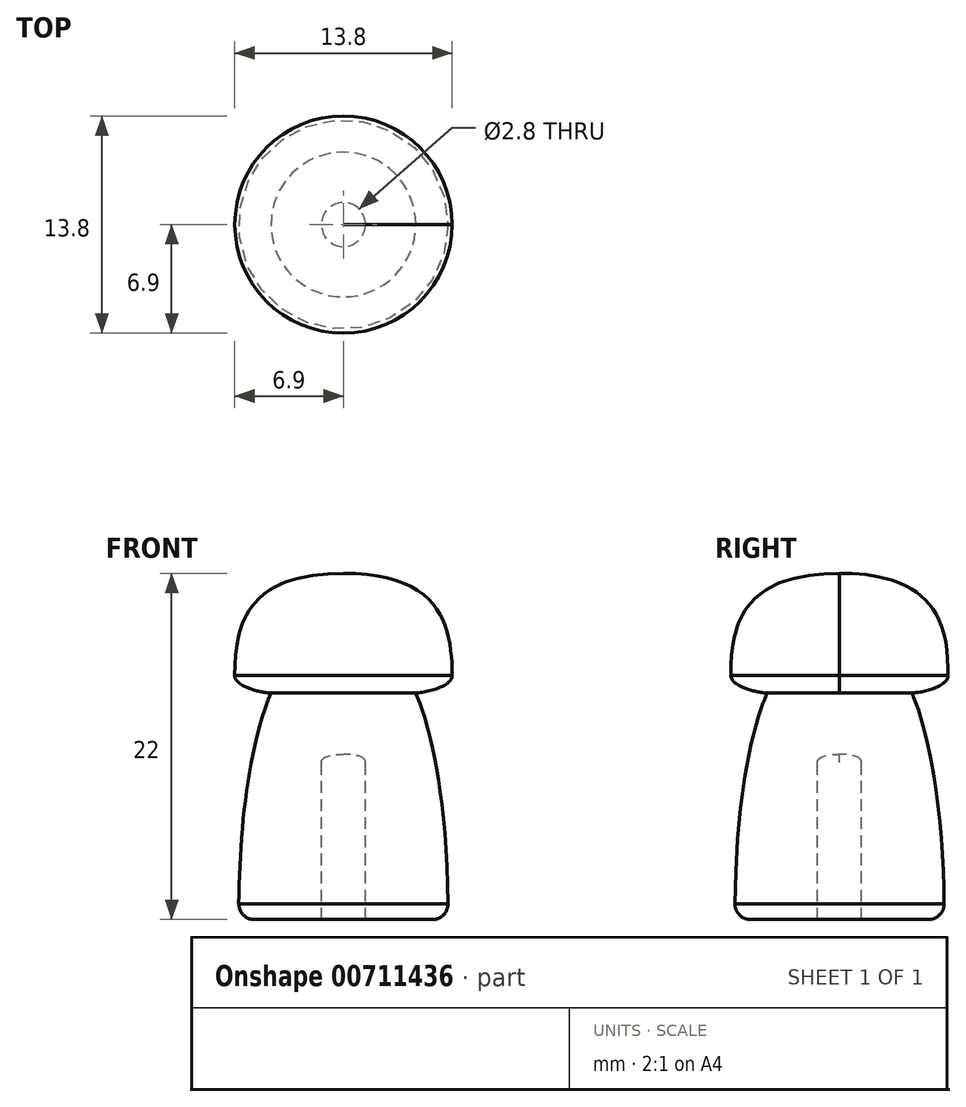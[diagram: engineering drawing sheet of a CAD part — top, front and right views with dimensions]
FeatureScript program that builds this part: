
annotation { "Feature Type Name" : "Feature", "Feature Type Description" : "" }
export const myFeature = defineFeature(function(context is Context, id is Id, definition is map)
    precondition{}
    {
        {
            var Q0;
            Q0=qCreatedBy(makeId("Front.planeOp"),FACE);
            var sketch = newSketch(context, id + "F0", { "sketchPlane" : qUnion([Q0])});
            skLineSegment(sketch, "E0", {"start": v(0, 25) * mm, "end": v(0, -25) * mm, "construction": true});
            skLineSegment(sketch, "E1", {"start": v(25, 0) * mm, "end": v(-25, 0) * mm, "construction": true});
            skLineSegment(sketch, "E2", {"start": v(1.4, 10) * mm, "end": v(1.4, 0) * mm});
            skFitSpline(sketch, "E3", {"points": [v(1.4, 10) * mm, v(0, 10.5) * mm], "startDerivative": vector(0, 1.5) * mm, "endDerivative": vector(-0.6, 0) * mm});
            skLineSegment(sketch, "E4", {"start": v(1.4, 0) * mm, "end": v(6.65, 0) * mm});
            skPoint(sketch, "E5", {"position": v(0, 22) * mm});
            skPoint(sketch, "E6", {"position": v(0, 14.4) * mm});
            skPoint(sketch, "E7", {"position": v(4.6, 14.4) * mm});
            skFitSpline(sketch, "E8", {"points": [v(4.6, 14.4) * mm, v(6.65, 0) * mm], "startDerivative": vector(0.2, -0.9) * mm, "endDerivative": vector(0, -30.95) * mm});
            skPoint(sketch, "E9", {"position": v(0, 15.5) * mm});
            skPoint(sketch, "E10", {"position": v(6.9, 15.5) * mm});
            skFitSpline(sketch, "E11", {"points": [v(4.6, 14.4) * mm, v(6.9, 15.5) * mm], "startDerivative": vector(1.88, 0) * mm, "endDerivative": vector(0, 2.1) * mm});
            skFitSpline(sketch, "E12", {"points": [v(0, 22) * mm, v(6.9, 15.5) * mm], "startDerivative": vector(18.86, 0) * mm, "endDerivative": vector(0, -9.19) * mm});
            skLineSegment(sketch, "E13", {"start": v(0, 22) * mm, "end": v(0, 10.5) * mm});
            skSolve(sketch);
        }
        {
            var Q0;
            Q0=makeQuery(id+"F0.imprint","IMPRINT",FACE,{"disambiguationData":[TD([[makeQuery(id+"F0.imprint","IMPRINT",EDGE,{"derivedFrom":sQuery(id+"F0.wireOp",EDGE,"E2")}),1.0]])]});
            var Q1;
            Q1=sQuery(id+"F0.wireOp",EDGE,"E12");
            var Q2;
            Q2=sQuery(id+"F0.wireOp",EDGE,"E11");
            var Q3;
            Q3=sQuery(id+"F0.wireOp",EDGE,"E8");
            var Q4;
            Q4=sQuery(id+"F0.wireOp",EDGE,"E2");
            var Q5;
            Q5=sQuery(id+"F0.wireOp",EDGE,"E4");
            var Q6;
            Q6=sQuery(id+"F0.wireOp",EDGE,"E3");
            var Q7;
            Q7=sQuery(id+"F0.wireOp",EDGE,"E0");
            revolve(context, id + "F1", {"surfaceOperationType" : NewSurfaceOperationType.NEW, "entities" : qUnion([Q0]), "surfaceEntities" : qUnion([Q1, Q2, Q3, Q4, Q5, Q6]), "axis" : qUnion([Q7]), "revolveType" : RevolveType.FULL});
        }
        {
            var Q0;
            Q0=makeQuery(id+"F1.opRevolve","SWEPT_EDGE",EDGE,{"disambiguationData":[OSD([sQuery(id+"F0.wireOp",EDGE,"E4"),sQuery(id+"F0.wireOp",EDGE,"E8")])]});
            fillet(context, id + "F2", {"entities" : qUnion([Q0]), "radius" : 1 * mm, "tangentPropagation" : true, "allowEdgeOverflow" : false});
        }
    });
